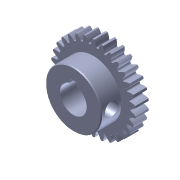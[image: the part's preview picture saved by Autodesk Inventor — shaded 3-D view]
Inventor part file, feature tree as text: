
AUTODESK INVENTOR PART (.ipt)
format: ipt  version: 2013 (Build 170138000, 138)  size: 361,472 bytes
history: native  units: in
note: dims shown in document units (in); Inventor stores cm internally (conversion verified against a paired STEP export)
features: chamfer x1, other x1, imported_body x1
ambient origin geometry x8: Origin, YZ Plane, XZ Plane, XY Plane, X Axis, Y Axis, Z Axis, Center Point
feature tree (3):
  chamfer  "Chamfer1"  [1 undecoded]
  other  "217-3141-006 Rev1_30T 32DP1"
  imported_body  "Base1"
note: 1 required parameter value undecoded (feature->parameter linkage not recoverable at this tier; creation-order binding heuristic only, values carry confidence <= 0.55)
